# Revit family: Q-SYS IO-8 Flex Surface Mount
name_source: partatom
category: Generic Models
revit_build: Autodesk Revit 2015 (Build: 20150511_0715(x64)
units: mm (PartAtom-declared; Revit-internal decimal feet)

## types (3) — shared parameters
Default Elevation = 0.000"
Depth = 9.430"
Description = Q-SYS Channel Expander
Heat Load Active = 70
Height = 1.750"
Manufacturer = QSC Audio Products, LLC
Model = I/O-8 Flex
Regulatory Compliance = FCC 47 CFR Part 15 Class A, IC ICES-003, CE (EN55032, EN55035), EU RoHS directive 2011/65/EU, WEEE directive 2012/19/EU, China RoHS directive GB/T26572, EAC, RTL
Weight Dimensional (lb) = 6
Width = 8.660"

## per-type parameters (varying)
| type | Current Draw | Manufacturer URL | Power Peak | Product Documentation Link | Product Page URL | URL |
| SPA2-200 @ 100VAC | 1.2 | http://www.qsc.com | 25.5 | https://www.qsc.com | https://www.qsc.com |  |
| SPA2-200 @ 120VAC | 1.5 | http://www.qscaudio.com | 180 | http://www.qsc.com | http://www.qsc.com | http://www.qsc.com |
| SPA2-200 @ 230VAC | 0.8 | http://www.qscaudio.com | 184 | http://www.qsc.com | http://www.qsc.com | http://www.qsc.com |

## geometry (parser evidence)
native form markers: Blend x2, Sweep x21
no freeform markers — native parametric forms only
